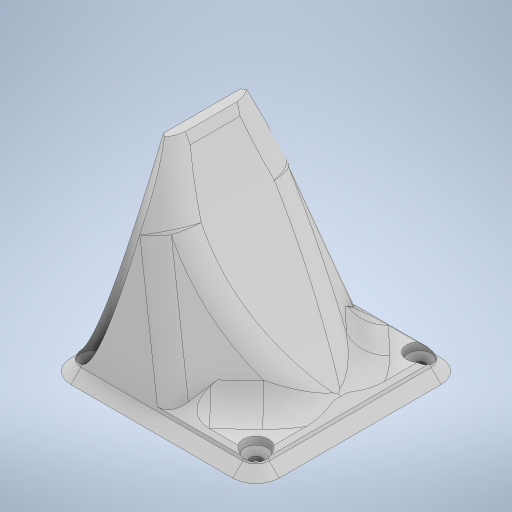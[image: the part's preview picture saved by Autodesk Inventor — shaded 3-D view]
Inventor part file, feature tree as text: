
AUTODESK INVENTOR PART (.ipt)
format: ipt  version: 2024.1 (Build 281209000, 209)  size: 520,192 bytes
history: native  units: mm
features: chamfer x8, fillet x6, extrude x5, sketch x5, projected_geometry x1
ambient origin geometry x8: Origin, YZ Plane, XZ Plane, XY Plane, X Axis, Y Axis, Z Axis, Center Point
bodies: Solid1 (feature_tree)
feature tree (25):
  extrude  "Extrusion1"  Depth=63.0mm
  extrude  "Extrusion2"  Depth=3.52mm
  fillet  "Fillet1"  Radius=49.5mm
  chamfer  "Chamfer1"  Distance=6.75mm
  chamfer  "Chamfer2"  Distance=6.75mm
  extrude  "Extrusion4"  TaperAngle=0.0deg  [1 undecoded]
  extrude  "Extrusion5"  Depth=10.0mm
  chamfer  "Chamfer7"  Distance=1.7mm Angle=45.0deg
  chamfer  "Chamfer8"  Distance=3.0mm Angle=45.0deg
  fillet  "Fillet5"  Radius=25.0mm
  fillet  "Fillet6"  Radius=8.0mm
  chamfer  "Chamfer6"  Distance=8.0mm
  extrude  "Extrusion3"  Depth=10.0mm TaperAngle=0.0deg
  chamfer  "Chamfer3"  Distance=20.0mm Angle=45.0deg
  chamfer  "Chamfer4"  Distance=10.0mm Angle=45.0deg
  chamfer  "Chamfer5"  Distance=5.0mm Angle=45.0deg
  fillet  "Fillet2"  Radius=7.0mm
  fillet  "Fillet3"  Radius=4.0mm
  fillet  "Fillet4"  Radius=6.0mm
  sketch  "Sketch1"  dims[d0=63.0mm d1=63.0mm]
  sketch  "Sketch2"  dims[d2=3.0mm d3=0.0mm d4=3.52mm d5=49.5mm]
  sketch  "Sketch3"  dims[d6=49.5mm]
  sketch  "Sketch5"  dims[d7=6.75mm]
  projected_geometry  "Projected Loop1"
  sketch  "Sketch7"  dims[d8=6.75mm d9=6.75mm d10=6.75mm d11=0.0mm d12=0.0mm d13=7.0mm d14=1.7mm d15=2.0mm d16=45.0deg d17=3.0mm d18=2.0mm d19=45.0deg d20=25.0mm d21=8.0mm d22=8.0mm d23=57.0mm d24=0.0mm d25=20.0mm d26=2.0mm d27=45.0deg d28=10.0mm d29=2.0mm d30=45.0deg d31=5.0mm d32=2.0mm d33=45.0deg d34=7.0mm d35=4.0mm d36=6.0mm d37=57.0mm d38=-2.094395mm d42=15.0mm d43=12.0mm d44=12.0mm d45=55.0mm d46=-3.490659mm d47=1.5mm d48=2.0mm d49=45.0deg d50=1.0mm d51=2.0mm d52=45.0deg d53=4.0mm d54=2.0mm d55=45.0deg d56=110.0mm d57=10.0mm]
note: 1 required parameter value undecoded (feature->parameter linkage not recoverable at this tier; creation-order binding heuristic only, values carry confidence <= 0.55)
